# Revit family: OXYTYP004
name_source: partatom
category: Furniture
units: mm (PartAtom-declared; Revit-internal decimal feet)

## family parameters
Always vertical = Yes
Cut with Voids When Loaded = No
OmniClass Number = 23.40.20.00
OmniClass Title = General Furniture and Specialties
Render Appearance Source = Family Geometry
Room Calculation Point = No
Shared = No
Work Plane-Based = No

## types (1)
- OXYTYP004
    Cost = 28874 $
    Default Elevation = 0 mm  [stored 0 ft]
    Description = 3 x BOX / FILE PEDESTAL MOBILE w/CUSHION 12"W, 2 x Duplex Outlet - Line 1 - Black, 2 x Duplex Outlet - Line 2 - Black, 1 x Duplex Outlet - Line 3 - Black, 1 x Duplex Outlet - Line 4 Dedicated - Black, 2 x 51 in. Electrical Jumper (Pt 30E), 1 x Oxygen Laminate Single End Panel Left 28Hx24D, 1 x Oxygen Laminate Single End Panel Right 28Hx24D, 3 x Unv. Spine Insert Screen - Glass .250 16H x 72W, 3 x Single Bench Powered w/Access Box Box 24D X 72W, 2 x Single Sided Shared Straight Leg Kit - 24D, 4 x Slimline Scrn,Terri,FVWL,Dim F,UMnt,Shrd,16hx24w, 3 x WESKO FILE BAR - 12"
    Exported From CET Designer = Yes
    Manufacturer = AIS
    Model = C-BFP1812M
    Show OXYTYP004 = Yes
    VisibilityIndex = 0

note: [stored X ft] marks values corroborated as IEEE doubles in the binary element streams (Revit-internal decimal feet)

## geometry (parser evidence)
native form markers: Sweep x3
no freeform markers — native parametric forms only
